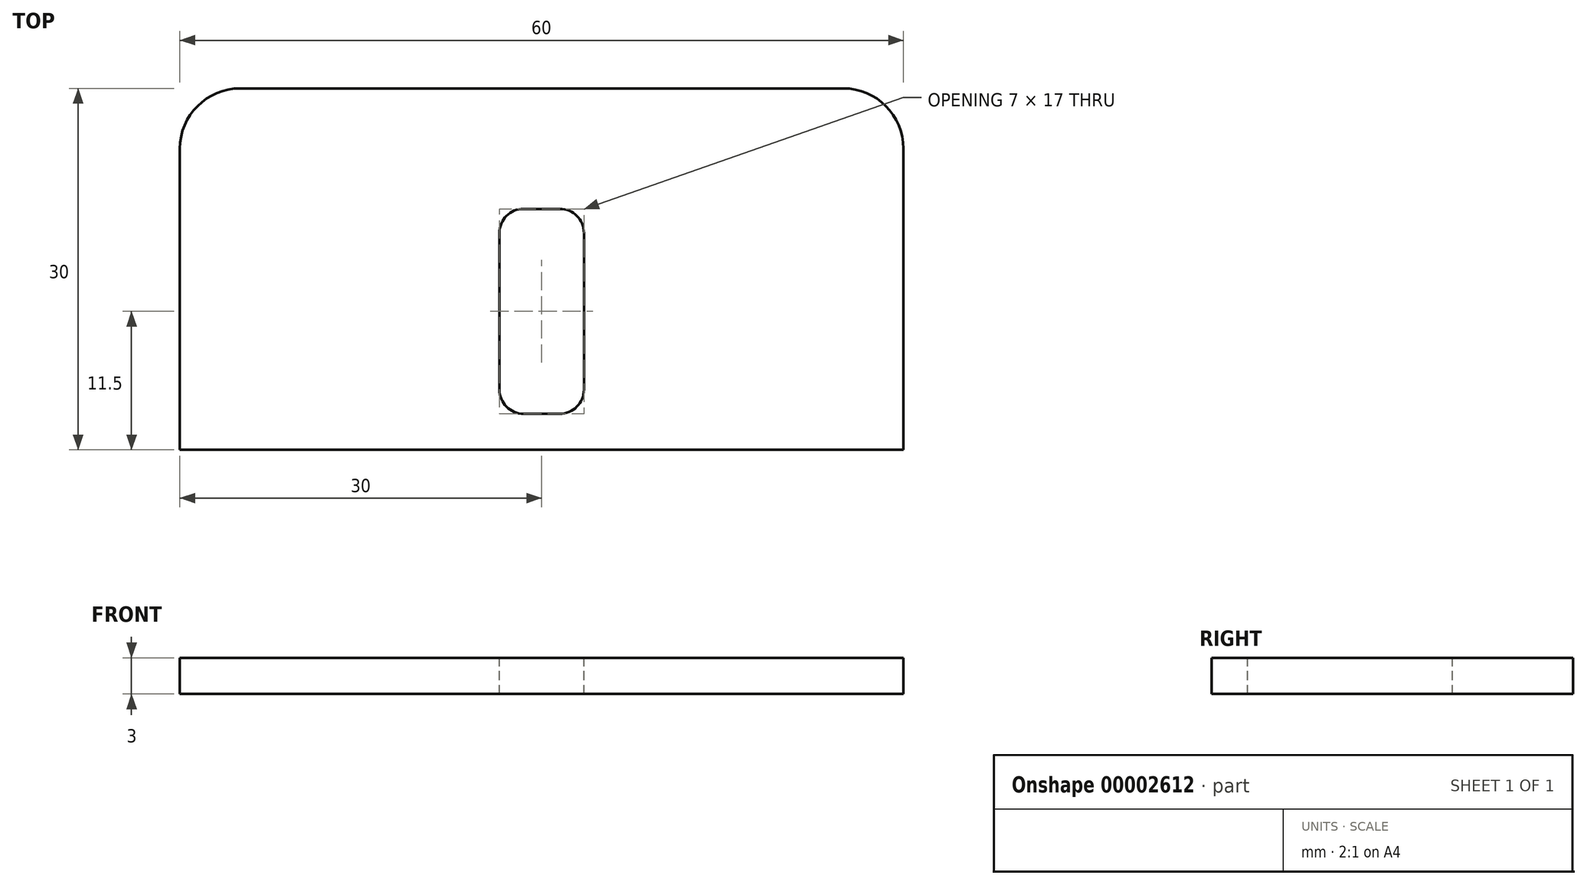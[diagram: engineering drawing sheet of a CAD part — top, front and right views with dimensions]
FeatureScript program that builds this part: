
annotation { "Feature Type Name" : "Feature", "Feature Type Description" : "" }
export const myFeature = defineFeature(function(context is Context, id is Id, definition is map)
    precondition{}
    {
        {
            var Q0;
            Q0=qCreatedBy(makeId("Top.planeOp"),FACE);
            var sketch = newSketch(context, id + "F0", { "sketchPlane" : qUnion([Q0])});
            skLineSegment(sketch, "E0.rect.bottom", {"start": v(-30, 15) * mm, "end": v(30, 15) * mm});
            skLineSegment(sketch, "E0.rect.top", {"start": v(-30, -15) * mm, "end": v(30, -15) * mm});
            skLineSegment(sketch, "E0.rect.left", {"start": v(-30, 15) * mm, "end": v(-30, -15) * mm});
            skLineSegment(sketch, "E0.rect.right", {"start": v(30, 15) * mm, "end": v(30, -15) * mm});
            skPoint(sketch, "E0.rect.middle", {"position": v(0, 0) * mm});
            skSolve(sketch);
        }
        {
            var Q0;
            Q0=makeQuery(id+"F0.imprint","IMPRINT",FACE,{"disambiguationData":[TD([[makeQuery(id+"F0.imprint","IMPRINT",EDGE,{"derivedFrom":sQuery(id+"F0.wireOp",EDGE,"E0.rect.bottom")}),-1.0]])]});
            extrude(context, id + "F1", {"entities" : qUnion([Q0]), "depth" : 3 * mm});
        }
        {
            var Q0;
            Q0=makeQuery(id+"F1.opExtrude","CAP_FACE",FACE,{"disambiguationData":[OSD([sQuery(id+"F0.wireOp",EDGE,"E0.rect.bottom"),sQuery(id+"F0.wireOp",EDGE,"E0.rect.top"),sQuery(id+"F0.wireOp",EDGE,"E0.rect.left"),sQuery(id+"F0.wireOp",EDGE,"E0.rect.right")])],"isStart":false});
            var sketch = newSketch(context, id + "F2", { "sketchPlane" : qUnion([Q0])});
            skLineSegment(sketch, "E1", {"start": v(0, 0) * mm, "end": v(-3.5, 0) * mm, "construction": true});
            skLineSegment(sketch, "E2", {"start": v(-3.5, 0) * mm, "end": v(-3.5, 5) * mm, "construction": true});
            skLineSegment(sketch, "E3", {"start": v(0, 0) * mm, "end": v(0, -12) * mm, "construction": true});
            skLineSegment(sketch, "E4", {"start": v(0, -12) * mm, "end": v(3.5, -12) * mm, "construction": true});
            skLineSegment(sketch, "E5.bottom", {"start": v(-3.5, 5) * mm, "end": v(3.5, 5) * mm});
            skLineSegment(sketch, "E5.top", {"start": v(-3.5, -12) * mm, "end": v(3.5, -12) * mm});
            skLineSegment(sketch, "E5.left", {"start": v(-3.5, 5) * mm, "end": v(-3.5, -12) * mm});
            skLineSegment(sketch, "E5.right", {"start": v(3.5, 5) * mm, "end": v(3.5, -12) * mm});
            skSolve(sketch);
        }
        {
            var Q0;
            Q0=makeQuery(id+"F2.imprint","IMPRINT",FACE,{"disambiguationData":[TD([[makeQuery(id+"F2.imprint","IMPRINT",EDGE,{"derivedFrom":sQuery(id+"F2.wireOp",EDGE,"E5.bottom")}),-1.0]])]});
            extrude(context, id + "F3", {"entities" : qUnion([Q0]), "operationType" : NewBodyOperationType.REMOVE, "oppositeDirection" : true, "depth" : 25 * mm});
        }
        {
            var Q0;
            Q0=makeQuery(id+"F3.boolean.opBoolean","COPY",EDGE,{"derivedFrom":makeQuery(id+"F3.opExtrude","SWEPT_EDGE",EDGE,{"disambiguationData":[OSD([sQuery(id+"F2.wireOp",EDGE,"E5.top"),sQuery(id+"F2.wireOp",EDGE,"E5.left")])]})});
            var Q1;
            Q1=makeQuery(id+"F3.boolean.opBoolean","COPY",EDGE,{"derivedFrom":makeQuery(id+"F3.opExtrude","SWEPT_EDGE",EDGE,{"disambiguationData":[OSD([sQuery(id+"F2.wireOp",EDGE,"E5.bottom"),sQuery(id+"F2.wireOp",EDGE,"E5.left")])]})});
            var Q2;
            Q2=makeQuery(id+"F3.boolean.opBoolean","COPY",EDGE,{"derivedFrom":makeQuery(id+"F3.opExtrude","SWEPT_EDGE",EDGE,{"disambiguationData":[OSD([sQuery(id+"F2.wireOp",EDGE,"E5.bottom"),sQuery(id+"F2.wireOp",EDGE,"E5.right")])]})});
            var Q3;
            Q3=makeQuery(id+"F3.boolean.opBoolean","COPY",EDGE,{"derivedFrom":makeQuery(id+"F3.opExtrude","SWEPT_EDGE",EDGE,{"disambiguationData":[OSD([sQuery(id+"F2.wireOp",EDGE,"E5.top"),sQuery(id+"F2.wireOp",EDGE,"E5.right")])]})});
            fillet(context, id + "F4", {"entities" : qUnion([Q0, Q1, Q2, Q3]), "radius" : 2 * mm, "tangentPropagation" : true, "allowEdgeOverflow" : false});
        }
        {
            var Q0;
            Q0=makeQuery(id+"F1.opExtrude","SWEPT_EDGE",EDGE,{"disambiguationData":[OSD([sQuery(id+"F0.wireOp",EDGE,"E0.rect.bottom"),sQuery(id+"F0.wireOp",EDGE,"E0.rect.left")])]});
            var Q1;
            Q1=makeQuery(id+"F1.opExtrude","SWEPT_EDGE",EDGE,{"disambiguationData":[OSD([sQuery(id+"F0.wireOp",EDGE,"E0.rect.bottom"),sQuery(id+"F0.wireOp",EDGE,"E0.rect.right")])]});
            fillet(context, id + "F5", {"entities" : qUnion([Q0, Q1]), "radius" : 5 * mm, "tangentPropagation" : true, "allowEdgeOverflow" : false});
        }
    });
